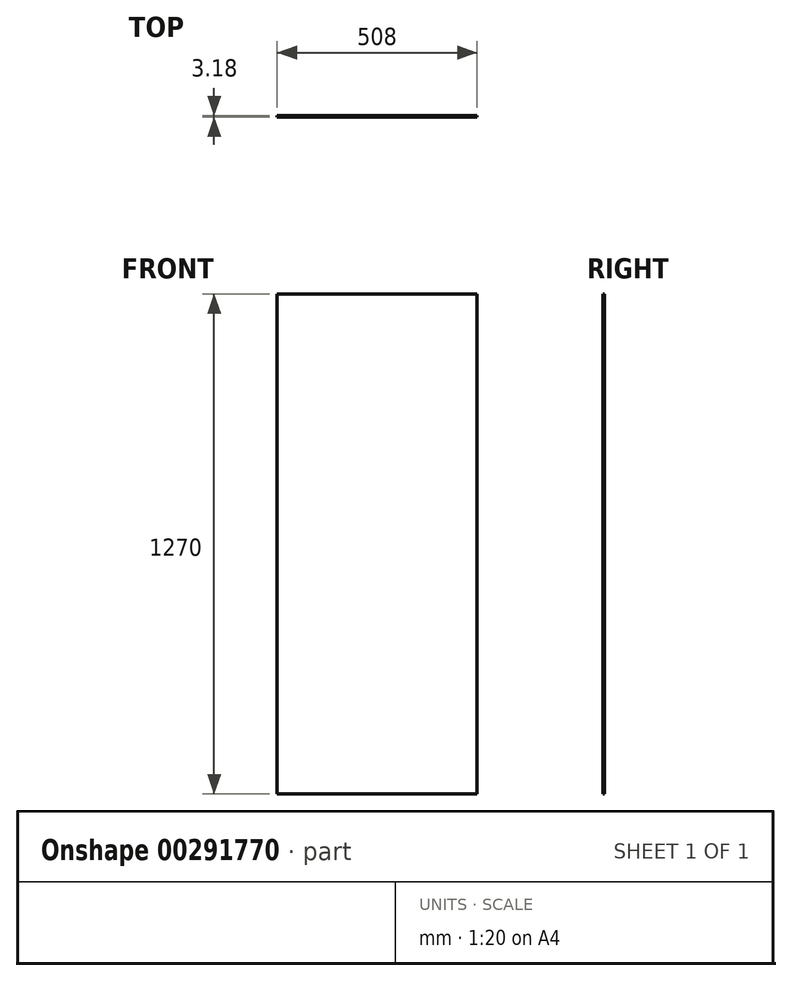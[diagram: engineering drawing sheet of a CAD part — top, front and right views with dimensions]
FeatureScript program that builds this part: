
annotation { "Feature Type Name" : "Feature", "Feature Type Description" : "" }
export const myFeature = defineFeature(function(context is Context, id is Id, definition is map)
    precondition{}
    {
        {
            var Q0;
            Q0=qCreatedBy(makeId("Front.planeOp"),FACE);
            var sketch = newSketch(context, id + "F0", { "sketchPlane" : qUnion([Q0])});
            skLineSegment(sketch, "E0.bottom", {"start": v(-213.34, 783.58) * mm, "end": v(294.66, 783.58) * mm});
            skLineSegment(sketch, "E0.top", {"start": v(-213.34, -486.42) * mm, "end": v(294.66, -486.42) * mm});
            skLineSegment(sketch, "E0.left", {"start": v(-213.34, 783.58) * mm, "end": v(-213.34, -486.42) * mm});
            skLineSegment(sketch, "E0.right", {"start": v(294.66, 783.58) * mm, "end": v(294.66, -486.42) * mm});
            skSolve(sketch);
        }
        {
            var Q0;
            Q0=makeQuery(id+"F0.imprint","IMPRINT",FACE,{"disambiguationData":[TD([[makeQuery(id+"F0.imprint","IMPRINT",EDGE,{"derivedFrom":sQuery(id+"F0.wireOp",EDGE,"E0.bottom")}),-1.0]])]});
            extrude(context, id + "F1", {"entities" : qUnion([Q0]), "endBound" : BoundingType.SYMMETRIC, "depth" : 3.17 * mm});
        }
    });
